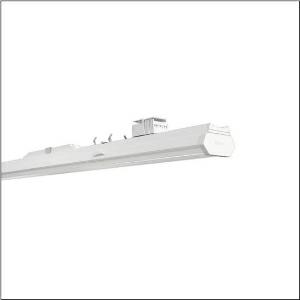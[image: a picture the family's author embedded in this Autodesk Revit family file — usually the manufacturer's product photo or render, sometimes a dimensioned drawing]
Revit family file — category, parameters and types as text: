
# Revit family: licross_r__21_protected_ho_52td11dn4e5s_21e0
name_source: partatom
category: Lighting Fixtures
units: mm (PartAtom-declared; Revit-internal decimal feet)

## family parameters
Cut with Voids When Loaded = No
Host = Face
Light Source = No
Part Type = Normal
Room Calculation Point = No
Round Connector Dimension = Use Diameter
Shared = No

## types (1)
- --- (1 x LED, 14920 lm, 84.9 W, 4000K)
    Apparent Load = 85 VA
    CIE Flux Codes = 84 94 98 99 100
    Color Rendering = 80
    Color Temperature = 4000K
    Default Elevation = 1800 mm
    Description = Licross® 21 Protected HO, luminaire insert, of sheet steel, galvanised, coil coated, white, length: 1.500mm, width: 90mm, height: 103mm, LED rated luminous flux: 14.920lm, light colour: 840, control gear: DALI 2, with plug, 5-pole, with phase selection, mains connection: 220..240V, AC, 50/60Hz, rated input power: 85W, halogen-free wiring, primary light control with lens, of plastic, primary optical cover: cover, of PMMA, light emission: direct distribution, primary light characteristic: symmetric, protection rating (complete): IP54, insulation class (complete): insulation class I (protective earthing), certification: CE, ENEC, VDE, UKCA, protection symbol: D if used in an environment with non-conductive dust loads with corresponding accessories, impact resistance: IK06, permissible ambient temperature for indoor applications: -25..+35°C, corresponds to IFS (International Featured Standards) requirements for safety and quality in the food industry, reducing of maximum allowable ambient temperature of 5°C with ceiling mounting, LABS conformity tested according to VDMA 24364:2018-05, packaging unit: 1 piece
    Height = 92 mm
    Lamp = 1 x LED
    Lamp Light Flux = 14920 lm
    Lamp Power = 84.9 W
    Lamp count = 1
    Length = 1500 mm
    Luminous efficacy = 176 lm/W
    Manufacturer = Siteco
    ModVariant = No
    Model = 52TD11DN4E5S
    Mounting Place = Ceiling
    Mounting Type = Pendant
    Number of Poles = 1
    OnlyDefault = Yes
    Power Factor = 1
    Product Name = Licross® 21 Protected HO
    Product group = luminaire insert
    ProductGroupID = 902
    Protection Class = Protection class I
    Protection Degree = IP 54
    RLX_Detail_Level = 1
    RLX_Emergency_Light_Flux = 0 lm
    RLX_Emergency_Type = 0
    RLX_Emergency_Type_DB = No
    RlxData = <blob elided: 24409 chars, md5=0ed7f117>
    Socket = socket
    Standby Power = 0 W
    System Light Flux = 14920 lm
    System Power = 85 W
    Type Comments = factory setting: luminous flux: 100 % | dim-lin: 254 | 484 mA
    Type Image = l_1256148.jpg
    URL = http://relux.com
    VarID = @adj_128548
    Voltage = 0 V
    Weight = 0.00 kg
    Width = 88 mm

## geometry (parser evidence)
native form markers: Blend x4, Sweep x9
no freeform markers — native parametric forms only
